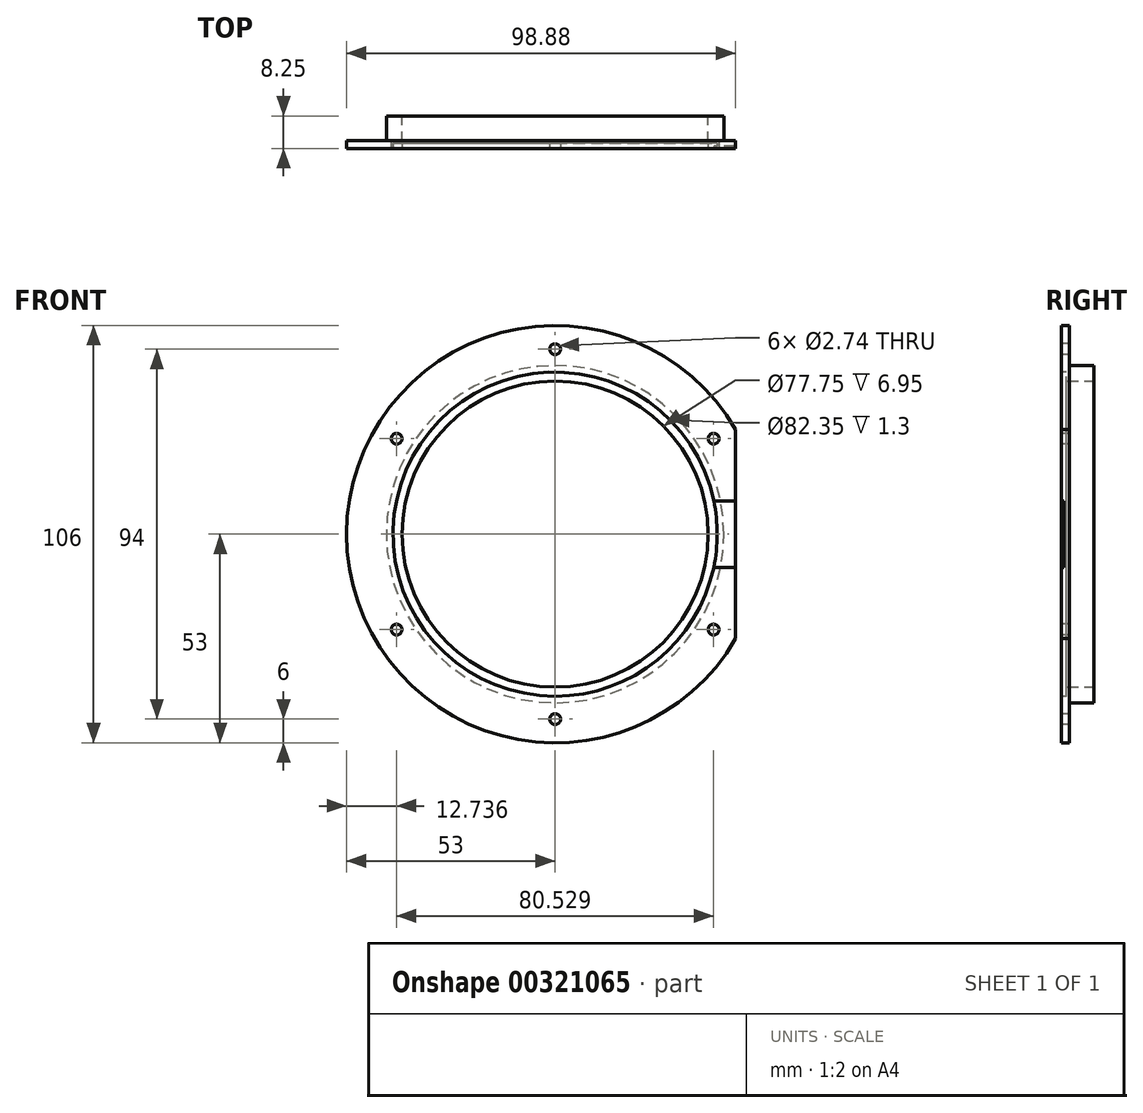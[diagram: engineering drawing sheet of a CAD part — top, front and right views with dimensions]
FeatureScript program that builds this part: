
annotation { "Feature Type Name" : "Feature", "Feature Type Description" : "" }
export const myFeature = defineFeature(function(context is Context, id is Id, definition is map)
    precondition{}
    {
        {
            var Q0;
            Q0=qCreatedBy(makeId("Front.planeOp"),FACE);
            var sketch = newSketch(context, id + "F0", { "sketchPlane" : qUnion([Q0])});
            skCircle(sketch, "E0", {"center": v(0, 0) * mm, "radius": 53 * mm});
            skCircle(sketch, "E1", {"center": v(0, 0) * mm, "radius": 38.88 * mm});
            skSolve(sketch);
        }
        {
            var Q0;
            Q0 = qSketchRegion(id + "F0", true);
            extrude(context, id + "F1", {"entities" : qUnion([Q0]), "depth" : 2 * mm});
        }
        {
            var Q0;
            Q0=makeQuery(id+"F1.opExtrude","CAP_FACE",FACE,{"disambiguationData":[OSD([sQuery(id+"F0.wireOp",EDGE,"E0"),sQuery(id+"F0.wireOp",EDGE,"E1")])],"isStart":false});
            var sketch = newSketch(context, id + "F2", { "sketchPlane" : qUnion([Q0])});
            skLineSegment(sketch, "E2.bottom", {"start": v(45.87, 70.2) * mm, "end": v(61.86, 70.2) * mm});
            skLineSegment(sketch, "E2.top", {"start": v(45.88, -29.8) * mm, "end": v(61.86, -29.8) * mm});
            skLineSegment(sketch, "E2.left", {"start": v(45.87, 70.2) * mm, "end": v(45.88, -29.8) * mm});
            skLineSegment(sketch, "E2.right", {"start": v(61.86, 70.2) * mm, "end": v(61.86, -29.8) * mm});
            skSolve(sketch);
        }
        {
            var Q0;
            Q0 = qSketchRegion(id + "F2", true);
            extrude(context, id + "F3", {"entities" : qUnion([Q0]), "operationType" : NewBodyOperationType.REMOVE, "oppositeDirection" : true, "depth" : 25 * mm});
        }
        {
            var Q0;
            Q0=makeQuery(id+"F1.opExtrude","CAP_FACE",FACE,{"disambiguationData":[OSD([sQuery(id+"F0.wireOp",EDGE,"E0"),sQuery(id+"F0.wireOp",EDGE,"E1")])],"isStart":false});
            var sketch = newSketch(context, id + "F4", { "sketchPlane" : qUnion([Q0])});
            skCircle(sketch, "E3", {"center": v(0, 0) * mm, "radius": 41.17 * mm});
            skSolve(sketch);
        }
        {
            var Q0;
            Q0 = qSketchRegion(id + "F4", true);
            extrude(context, id + "F5", {"entities" : qUnion([Q0]), "operationType" : NewBodyOperationType.REMOVE, "oppositeDirection" : true, "depth" : 1.3 * mm});
        }
        {
            var Q0;
            Q0=makeQuery(id+"F1.opExtrude","CAP_FACE",FACE,{"disambiguationData":[OSD([sQuery(id+"F0.wireOp",EDGE,"E0"),sQuery(id+"F0.wireOp",EDGE,"E1")])],"isStart":true});
            var sketch = newSketch(context, id + "F6", { "sketchPlane" : qUnion([Q0])});
            skCircle(sketch, "E4", {"center": v(0, 0) * mm, "radius": 38.88 * mm});
            skCircle(sketch, "E5", {"center": v(0, 0) * mm, "radius": 42.86 * mm});
            skSolve(sketch);
        }
        {
            var Q0;
            Q0 = qSketchRegion(id + "F6", true);
            extrude(context, id + "F7", {"entities" : qUnion([Q0]), "operationType" : NewBodyOperationType.ADD, "depth" : 6.25 * mm});
        }
        {
            var Q0;
            Q0=makeQuery(id+"F1.opExtrude","CAP_FACE",FACE,{"disambiguationData":[OSD([sQuery(id+"F0.wireOp",EDGE,"E0"),sQuery(id+"F0.wireOp",EDGE,"E1")])],"isStart":false});
            var sketch = newSketch(context, id + "F8", { "sketchPlane" : qUnion([Q0])});
            skCircle(sketch, "E6", {"center": v(0, 0) * mm, "radius": 47 * mm, "construction": true});
            skCircle(sketch, "E7", {"center": v(0, 47) * mm, "radius": 1.37 * mm});
            skCircle(sketch, "E8", {"center": v(0, -47) * mm, "radius": 1.37 * mm});
            skCircle(sketch, "E9", {"center": v(40.26, 24.24) * mm, "radius": 1.37 * mm});
            skCircle(sketch, "E10", {"center": v(-40.26, 24.24) * mm, "radius": 1.37 * mm});
            skCircle(sketch, "E11", {"center": v(-40.26, -24.24) * mm, "radius": 1.37 * mm});
            skCircle(sketch, "E12", {"center": v(40.26, -24.24) * mm, "radius": 1.37 * mm});
            skSolve(sketch);
        }
        {
            var Q0;
            Q0 = qSketchRegion(id + "F8", true);
            extrude(context, id + "F9", {"entities" : qUnion([Q0]), "operationType" : NewBodyOperationType.REMOVE, "oppositeDirection" : true, "depth" : 25 * mm});
        }
        {
            var Q0;
            Q0=makeQuery(id+"F1.opExtrude","CAP_FACE",FACE,{"disambiguationData":[OSD([sQuery(id+"F0.wireOp",EDGE,"E0"),sQuery(id+"F0.wireOp",EDGE,"E1")])],"isStart":false});
            var sketch = newSketch(context, id + "F10", { "sketchPlane" : qUnion([Q0])});
            skLineSegment(sketch, "E13.bottom", {"start": v(51.15, 8.43) * mm, "end": v(35, 8.43) * mm});
            skLineSegment(sketch, "E13.top", {"start": v(51.15, -8.43) * mm, "end": v(35, -8.43) * mm});
            skLineSegment(sketch, "E13.left", {"start": v(51.15, 8.43) * mm, "end": v(51.15, -8.43) * mm});
            skLineSegment(sketch, "E13.right", {"start": v(35, 8.43) * mm, "end": v(35, -8.43) * mm});
            skPoint(sketch, "E13.middle", {"position": v(43.07, 0) * mm});
            skSolve(sketch);
        }
        {
            var Q0;
            Q0 = qSketchRegion(id + "F10", true);
            extrude(context, id + "F11", {"entities" : qUnion([Q0]), "operationType" : NewBodyOperationType.REMOVE, "oppositeDirection" : true, "depth" : .65 * mm});
        }
    });
